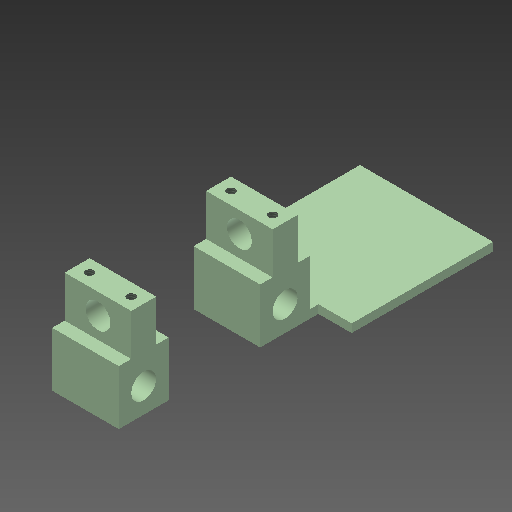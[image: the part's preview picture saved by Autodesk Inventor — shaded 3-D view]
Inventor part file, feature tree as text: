
AUTODESK INVENTOR PART (.ipt)
format: ipt  version: 2020 (Build 240168000, 168)  size: 218,112 bytes
history: native  units: mm
features: extrude x6, projected_geometry x5, thread x4, other x1, pattern_linear x1
ambient origin geometry x8: Origin, YZ Plane, XZ Plane, XY Plane, X Axis, Y Axis, Z Axis, Center Point
bodies: Body1 (feature_tree)
feature tree (17):
  other  "實體1"
  extrude  "Extrusion1"  Depth=3.0mm
  pattern_linear  "Rectangular Pattern1"  Spacing1=5.0mm  [1 undecoded]
  extrude  "Extrusion2"  Depth=3.0mm TaperAngle=0.0deg
  extrude  "Extrusion3"  Depth=20.0mm
  extrude  "Extrusion4"  Depth=6.05mm
  extrude  "Extrusion5"  Depth=3.0mm
  extrude  "Extrusion6"  Depth=3.0mm
  thread  "Thread1"  [1 undecoded]
  thread  "Thread2"  [1 undecoded]
  thread  "Thread3"  [1 undecoded]
  thread  "Thread4"  [1 undecoded]
  projected_geometry  "Projected Loop1"
  projected_geometry  "Projected Loop2"
  projected_geometry  "Projected Loop3"
  projected_geometry  "Projected Loop4"
  projected_geometry  "Projected Loop5"
note: 5 required parameter values undecoded (feature->parameter linkage not recoverable at this tier; creation-order binding heuristic only, values carry confidence <= 0.55)
